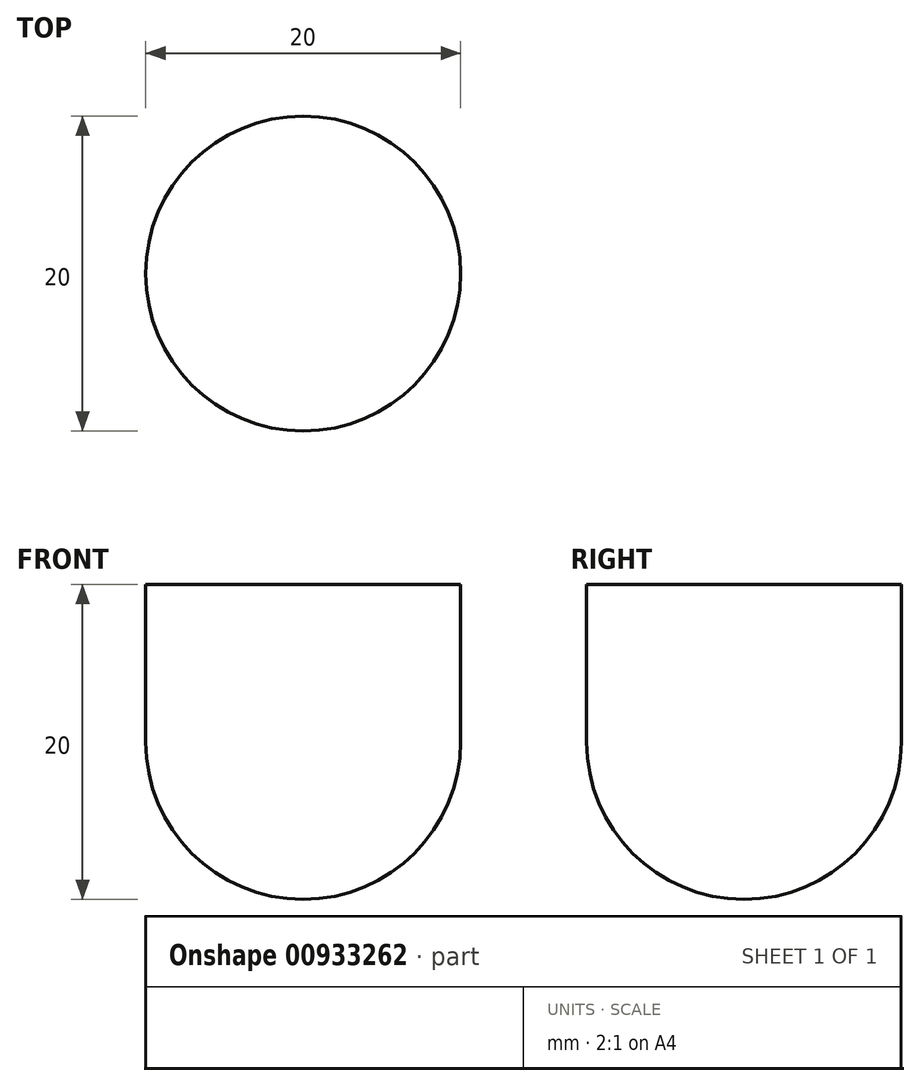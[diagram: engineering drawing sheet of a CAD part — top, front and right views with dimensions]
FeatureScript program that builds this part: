
annotation { "Feature Type Name" : "Feature", "Feature Type Description" : "" }
export const myFeature = defineFeature(function(context is Context, id is Id, definition is map)
    precondition{}
    {
        {
            var Q0;
            Q0=qCreatedBy(makeId("Top.planeOp"),FACE);
            var sketch = newSketch(context, id + "F0", { "sketchPlane" : qUnion([Q0])});
            skCircle(sketch, "E0", {"center": v(0, 0) * mm, "radius": 10 * mm});
            skLineSegment(sketch, "E1", {"start": v(0, 10) * mm, "end": v(0, -10) * mm});
            skSolve(sketch);
        }
        {
            var Q0;
            {var subQ0=sQuery(id+"F0.wireOp",EDGE,"E1");Q0=makeQuery(id+"F0.imprint","IMPRINT",FACE,{"disambiguationData":[TD([[makeQuery(id+"F0.imprint","IMPRINT",EDGE,{"derivedFrom":subQ0}),-1.0]])]});}
            var Q1;
            Q1=sQuery(id+"F0.wireOp",EDGE,"E1");
            revolve(context, id + "F1", {"surfaceOperationType" : NewSurfaceOperationType.NEW, "entities" : qUnion([Q0]), "axis" : qUnion([Q1]), "revolveType" : RevolveType.ONE_DIRECTION, "angle" : 180 * degree});
        }
        {
            var Q0;
            Q0=makeQuery(id+"F1.opRevolve","CAP_FACE",FACE,{"disambiguationData":[OSD([sQuery(id+"F0.wireOp",EDGE,"E0"),sQuery(id+"F0.wireOp",EDGE,"E1")])],"isStart":false});
            extrude(context, id + "F2", {"entities" : qUnion([Q0]), "operationType" : NewBodyOperationType.ADD, "depth" : 10 * mm, "offsetDistance" : 25 * mm});
        }
    });
